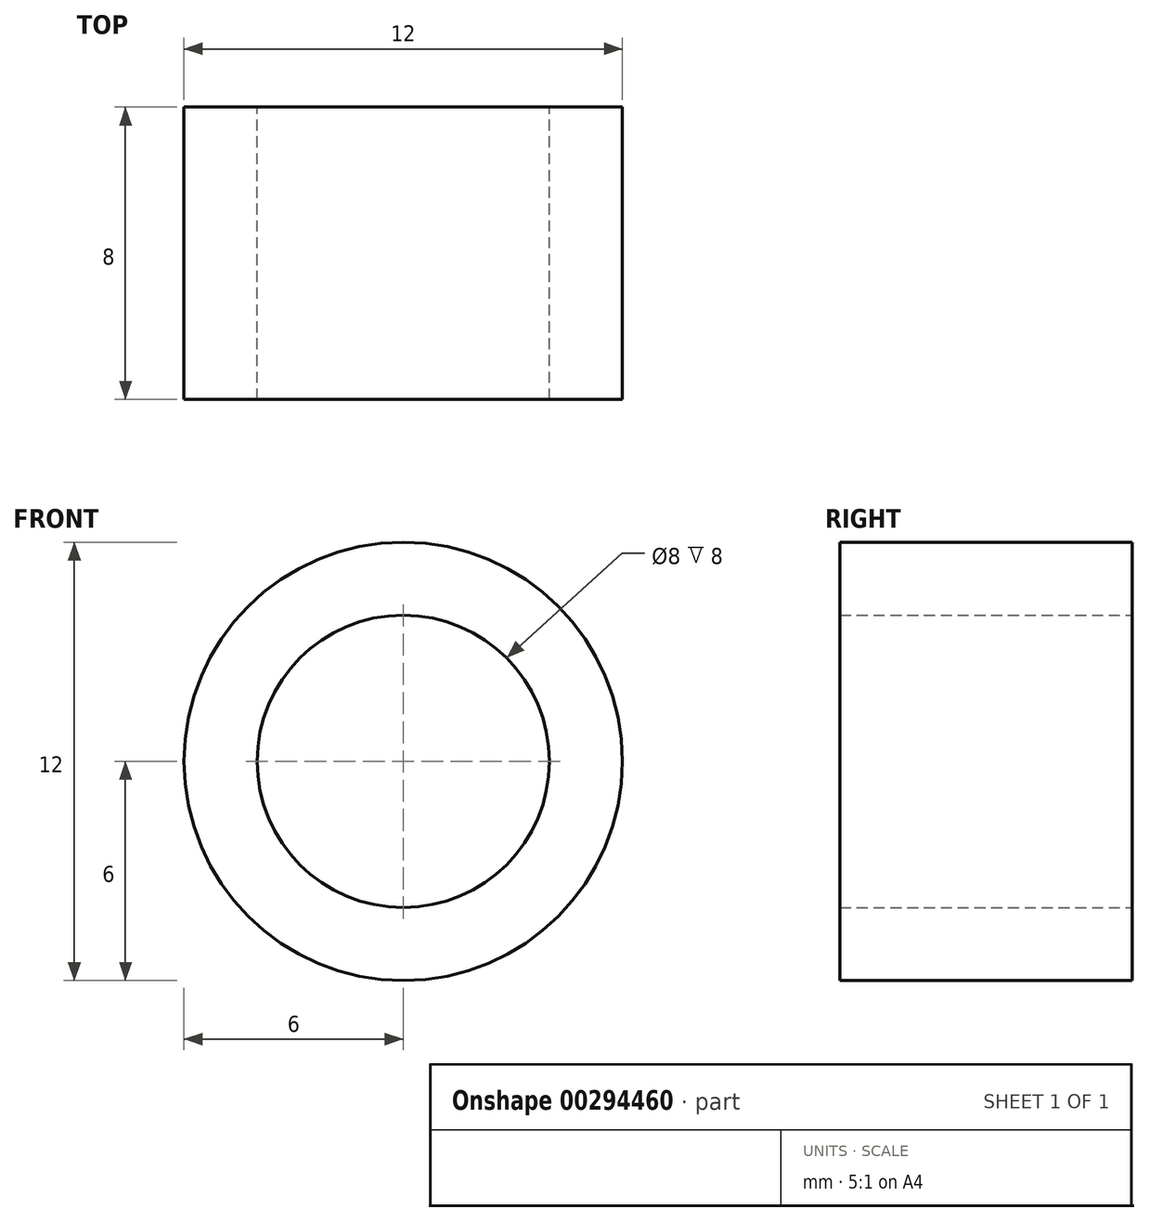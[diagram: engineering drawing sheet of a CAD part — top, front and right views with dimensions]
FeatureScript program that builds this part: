
annotation { "Feature Type Name" : "Feature", "Feature Type Description" : "" }
export const myFeature = defineFeature(function(context is Context, id is Id, definition is map)
    precondition{}
    {
        {
            var Q0;
            Q0=qCreatedBy(makeId("Front.planeOp"),FACE);
            var sketch = newSketch(context, id + "F0", { "sketchPlane" : qUnion([Q0])});
            skCircle(sketch, "E0", {"center": v(0, 0) * mm, "radius": 4 * mm});
            skCircle(sketch, "E1", {"center": v(0, 0) * mm, "radius": 6 * mm});
            skSolve(sketch);
        }
        {
            var Q0;
            Q0=makeQuery(id+"F0.imprint","IMPRINT",FACE,{"disambiguationData":[TD([[makeQuery(id+"F0.imprint","IMPRINT",EDGE,{"derivedFrom":sQuery(id+"F0.wireOp",EDGE,"E0")}),-1.0]])]});
            extrude(context, id + "F1", {"entities" : qUnion([Q0]), "depth" : 8 * mm});
        }
    });
